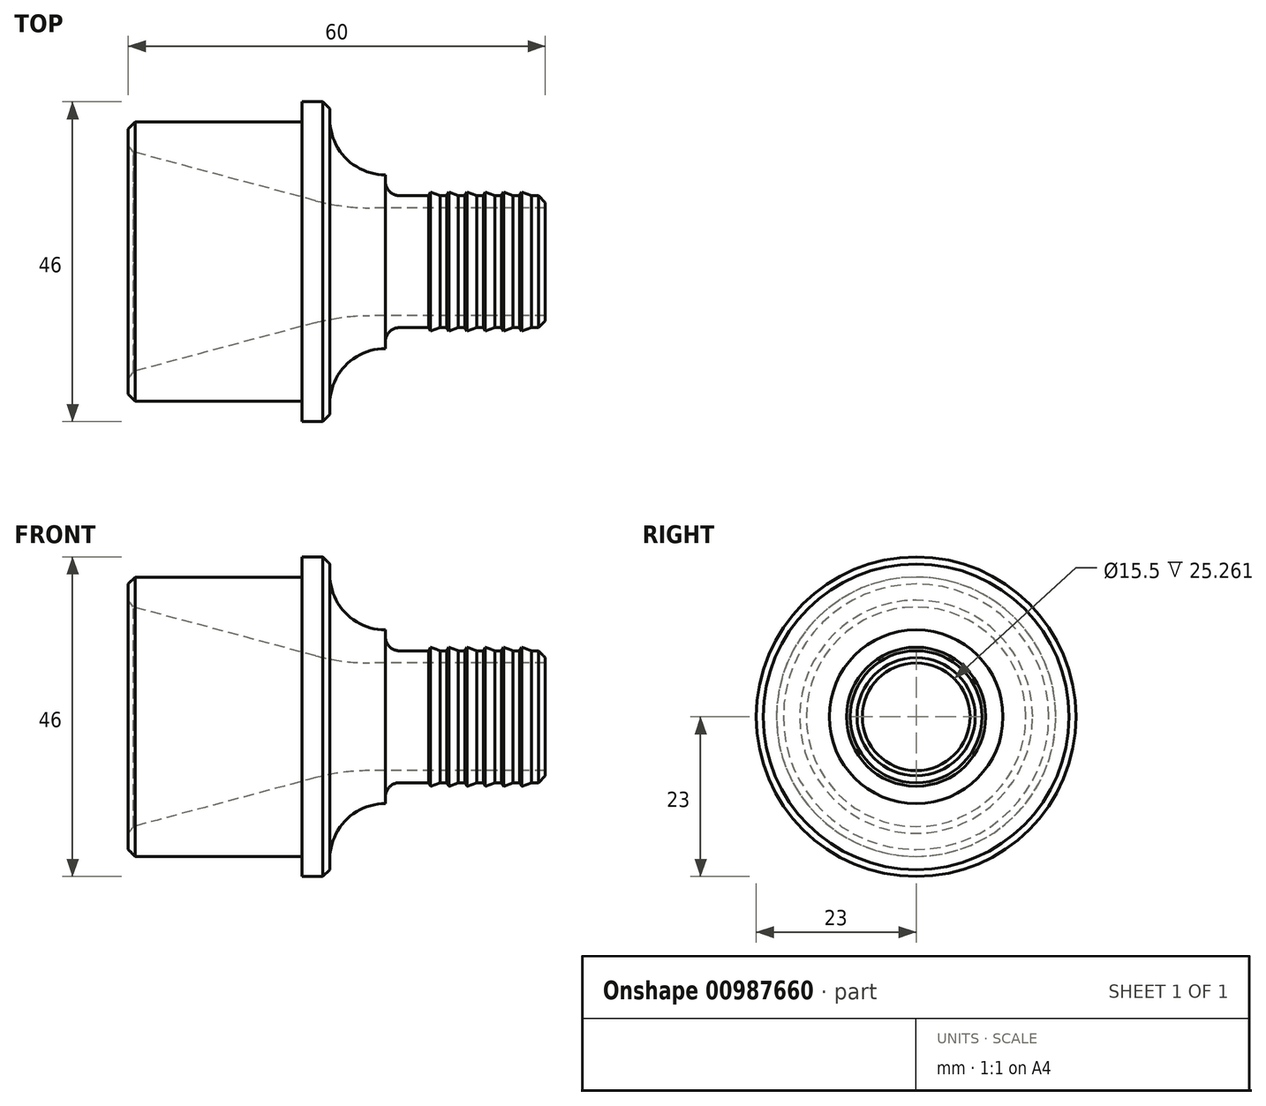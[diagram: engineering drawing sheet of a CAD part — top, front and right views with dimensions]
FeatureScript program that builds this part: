
annotation { "Feature Type Name" : "Feature", "Feature Type Description" : "" }
export const myFeature = defineFeature(function(context is Context, id is Id, definition is map)
    precondition{}
    {
        {
            var Q0;
            Q0=qCreatedBy(makeId("Front.planeOp"),FACE);
            var sketch = newSketch(context, id + "F0", { "sketchPlane" : qUnion([Q0])});
            skLineSegment(sketch, "E0", {"start": v(0, 0) * mm, "end": v(60, 0) * mm, "construction": true});
            skLineSegment(sketch, "E1", {"start": v(60, 9.5) * mm, "end": v(58, 9.5) * mm});
            skLineSegment(sketch, "E2", {"start": v(58, 9.5) * mm, "end": v(56.63, 10) * mm});
            skLineSegment(sketch, "E3", {"start": v(56.63, 10) * mm, "end": v(56.63, 9.5) * mm});
            skLineSegment(sketch, "E4", {"start": v(56.63, 9.5) * mm, "end": v(55.38, 9.5) * mm});
            skLineSegment(sketch, "E5", {"start": v(55.38, 9.5) * mm, "end": v(54, 10) * mm});
            skLineSegment(sketch, "E6", {"start": v(54, 10) * mm, "end": v(54, 9.5) * mm});
            skLineSegment(sketch, "E7", {"start": v(29, 12.5) * mm, "end": v(29, 23) * mm});
            skLineSegment(sketch, "E8", {"start": v(29, 23) * mm, "end": v(25, 23) * mm});
            skLineSegment(sketch, "E9", {"start": v(25, 23) * mm, "end": v(25, 20.1) * mm});
            skLineSegment(sketch, "E10", {"start": v(25, 20.1) * mm, "end": v(0, 20.1) * mm});
            skLineSegment(sketch, "E11", {"start": v(0, 20.1) * mm, "end": v(0, 16) * mm});
            skLineSegment(sketch, "E12", {"start": v(0, 16) * mm, "end": v(30.79, 7.75) * mm});
            skLineSegment(sketch, "E13", {"start": v(30.79, 7.75) * mm, "end": v(60, 7.75) * mm});
            skLineSegment(sketch, "E14", {"start": v(60, 7.75) * mm, "end": v(60, 9.5) * mm});
            skLineSegment(sketch, "E15", {"start": v(37, 9.5) * mm, "end": v(37, 12.5) * mm});
            skLineSegment(sketch, "E16", {"start": v(37, 12.5) * mm, "end": v(29, 12.5) * mm});
            skLineSegment(sketch, "E17", {"start": v(54, 9.5) * mm, "end": v(52.75, 9.5) * mm});
            skLineSegment(sketch, "E18.1.0.0", {"start": v(48.76, 9.5) * mm, "end": v(47.5, 9.5) * mm});
            skLineSegment(sketch, "E18.1.0.1", {"start": v(48.76, 10) * mm, "end": v(48.76, 9.5) * mm});
            skLineSegment(sketch, "E18.1.0.2", {"start": v(50.13, 9.5) * mm, "end": v(48.76, 10) * mm});
            skLineSegment(sketch, "E18.1.0.3", {"start": v(51.38, 9.5) * mm, "end": v(50.13, 9.5) * mm});
            skLineSegment(sketch, "E18.1.0.4", {"start": v(51.38, 10) * mm, "end": v(51.38, 9.5) * mm});
            skLineSegment(sketch, "E18.1.0.5", {"start": v(52.75, 9.5) * mm, "end": v(51.38, 10) * mm});
            skLineSegment(sketch, "E18.2.0.0", {"start": v(43.5, 9.5) * mm, "end": v(37, 9.5) * mm});
            skLineSegment(sketch, "E18.2.0.1", {"start": v(43.5, 10) * mm, "end": v(43.5, 9.5) * mm});
            skLineSegment(sketch, "E18.2.0.2", {"start": v(44.88, 9.5) * mm, "end": v(43.5, 10) * mm});
            skLineSegment(sketch, "E18.2.0.3", {"start": v(46.13, 9.5) * mm, "end": v(44.88, 9.5) * mm});
            skLineSegment(sketch, "E18.2.0.4", {"start": v(46.13, 10) * mm, "end": v(46.13, 9.5) * mm});
            skLineSegment(sketch, "E18.2.0.5", {"start": v(47.5, 9.5) * mm, "end": v(46.13, 10) * mm});
            skSolve(sketch);
        }
        {
            var Q0;
            Q0 = qSketchRegion(id + "F0", true);
            var Q1;
            Q1=sQuery(id+"F0.wireOp",EDGE,"E0");
            revolve(context, id + "F1", {"surfaceOperationType" : NewSurfaceOperationType.NEW, "entities" : qUnion([Q0]), "axis" : qUnion([Q1]), "revolveType" : RevolveType.FULL});
        }
        {
            var Q0;
            Q0=makeQuery(id+"F1.opRevolve","SWEPT_EDGE",EDGE,{"disambiguationData":[OSD([sQuery(id+"F0.wireOp",EDGE,"E7"),sQuery(id+"F0.wireOp",EDGE,"E16")])]});
            fillet(context, id + "F2", {"entities" : qUnion([Q0]), "radius" : 8 * mm, "tangentPropagation" : true, "allowEdgeOverflow" : false});
        }
        {
            var Q0;
            Q0=makeQuery(id+"F1.opRevolve","SWEPT_EDGE",EDGE,{"disambiguationData":[OSD([sQuery(id+"F0.wireOp",EDGE,"E1"),sQuery(id+"F0.wireOp",EDGE,"E14")])]});
            chamfer(context, id + "F3", {"entities" : qUnion([Q0]), "width" : 1 * mm, "tangentPropagation" : true});
        }
        {
            var Q0;
            Q0=makeQuery(id+"F1.opRevolve","SWEPT_EDGE",EDGE,{"disambiguationData":[OSD([sQuery(id+"F0.wireOp",EDGE,"E12"),sQuery(id+"F0.wireOp",EDGE,"E13")])]});
            fillet(context, id + "F4", {"entities" : qUnion([Q0]), "radius" : 30 * mm, "tangentPropagation" : true, "allowEdgeOverflow" : false});
        }
        {
            var Q0;
            Q0=makeQuery(id+"F1.opRevolve","SWEPT_EDGE",EDGE,{"disambiguationData":[OSD([sQuery(id+"F0.wireOp",EDGE,"E10"),sQuery(id+"F0.wireOp",EDGE,"E11")])]});
            var Q1;
            Q1=makeQuery(id+"F1.opRevolve","SWEPT_EDGE",EDGE,{"disambiguationData":[OSD([sQuery(id+"F0.wireOp",EDGE,"E11"),sQuery(id+"F0.wireOp",EDGE,"E12")])]});
            var Q2;
            Q2=makeQuery(id+"F1.opRevolve","SWEPT_EDGE",EDGE,{"disambiguationData":[OSD([sQuery(id+"F0.wireOp",EDGE,"E7"),sQuery(id+"F0.wireOp",EDGE,"E8")])]});
            chamfer(context, id + "F5", {"entities" : qUnion([Q0, Q1, Q2]), "width" : 1 * mm, "tangentPropagation" : true});
        }
        {
            var Q0;
            Q0=makeQuery(id+"F1.opRevolve","SWEPT_EDGE",EDGE,{"disambiguationData":[OSD([sQuery(id+"F0.wireOp",EDGE,"E15"),sQuery(id+"F0.wireOp",EDGE,"E18.2.0.0")])]});
            fillet(context, id + "F6", {"entities" : qUnion([Q0]), "radius" : 2 * mm, "tangentPropagation" : true, "allowEdgeOverflow" : false});
        }
        {
            var Q0;
            Q0=makeQuery(id+"F1.opRevolve","SWEPT_EDGE",EDGE,{"disambiguationData":[OSD([sQuery(id+"F0.wireOp",EDGE,"E6"),sQuery(id+"F0.wireOp",EDGE,"E17")])]});
            var Q1;
            Q1=makeQuery(id+"F1.opRevolve","SWEPT_EDGE",EDGE,{"disambiguationData":[OSD([sQuery(id+"F0.wireOp",EDGE,"E3"),sQuery(id+"F0.wireOp",EDGE,"E4")])]});
            var Q2;
            Q2=makeQuery(id+"F1.opRevolve","SWEPT_EDGE",EDGE,{"disambiguationData":[OSD([sQuery(id+"F0.wireOp",EDGE,"E18.1.0.3"),sQuery(id+"F0.wireOp",EDGE,"E18.1.0.4")])]});
            var Q3;
            Q3=makeQuery(id+"F1.opRevolve","SWEPT_EDGE",EDGE,{"disambiguationData":[OSD([sQuery(id+"F0.wireOp",EDGE,"E18.1.0.0"),sQuery(id+"F0.wireOp",EDGE,"E18.1.0.1")])]});
            var Q4;
            Q4=makeQuery(id+"F1.opRevolve","SWEPT_EDGE",EDGE,{"disambiguationData":[OSD([sQuery(id+"F0.wireOp",EDGE,"E18.2.0.3"),sQuery(id+"F0.wireOp",EDGE,"E18.2.0.4")])]});
            var Q5;
            Q5=makeQuery(id+"F1.opRevolve","SWEPT_EDGE",EDGE,{"disambiguationData":[OSD([sQuery(id+"F0.wireOp",EDGE,"E18.2.0.0"),sQuery(id+"F0.wireOp",EDGE,"E18.2.0.1")])]});
            chamfer(context, id + "F7", {"entities" : qUnion([Q0, Q1, Q2, Q3, Q4, Q5]), "chamferType" : ChamferType.OFFSET_ANGLE, "width" : 0.3 * mm, "oppositeDirection" : false, "angle" : 60 * degree, "tangentPropagation" : true});
        }
    });
